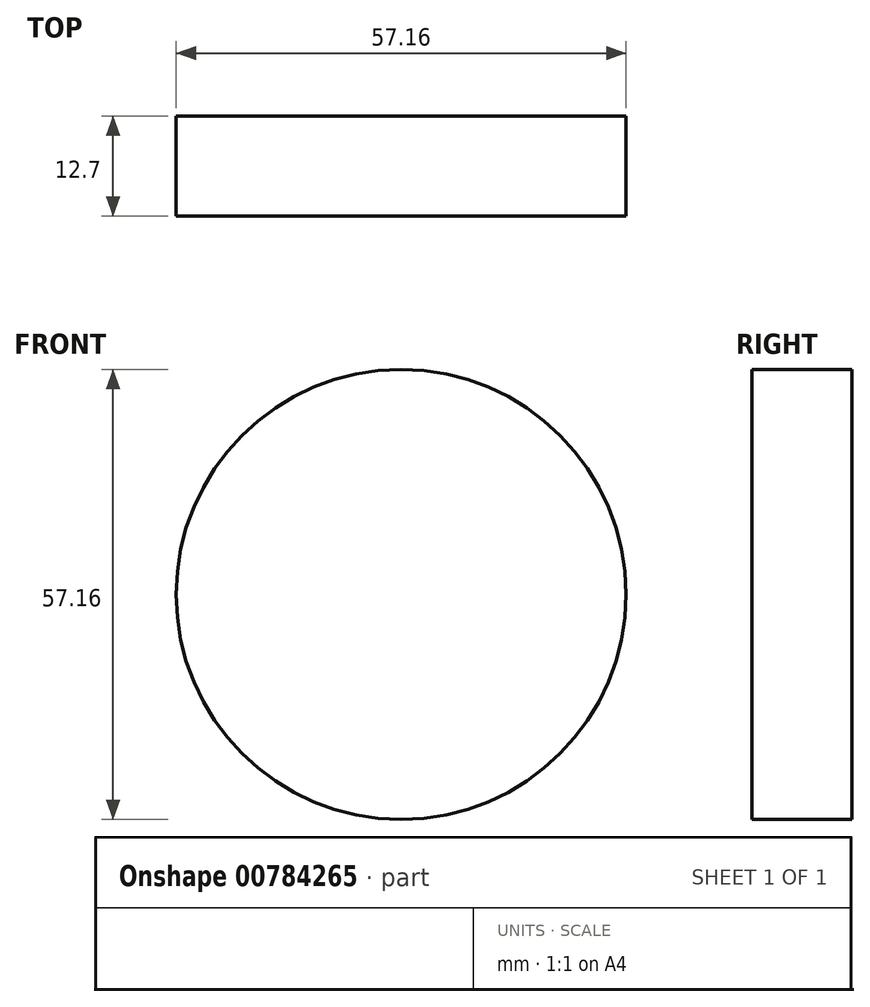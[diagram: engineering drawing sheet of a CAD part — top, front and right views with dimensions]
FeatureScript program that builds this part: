
annotation { "Feature Type Name" : "Feature", "Feature Type Description" : "" }
export const myFeature = defineFeature(function(context is Context, id is Id, definition is map)
    precondition{}
    {
        {
            var Q0;
            Q0=qCreatedBy(makeId("Front.planeOp"),FACE);
            var sketch = newSketch(context, id + "F0", { "sketchPlane" : qUnion([Q0])});
            skCircle(sketch, "E0", {"center": v(0, 0) * mm, "radius": 28.58 * mm});
            skSolve(sketch);
        }
        {
            var Q0;
            Q0 = qSketchRegion(id + "F0", true);
            extrude(context, id + "F1", {"entities" : qUnion([Q0]), "endBound" : BoundingType.SYMMETRIC, "depth" : 12.7 * mm, "offsetDistance" : 25.4 * mm});
        }
    });
